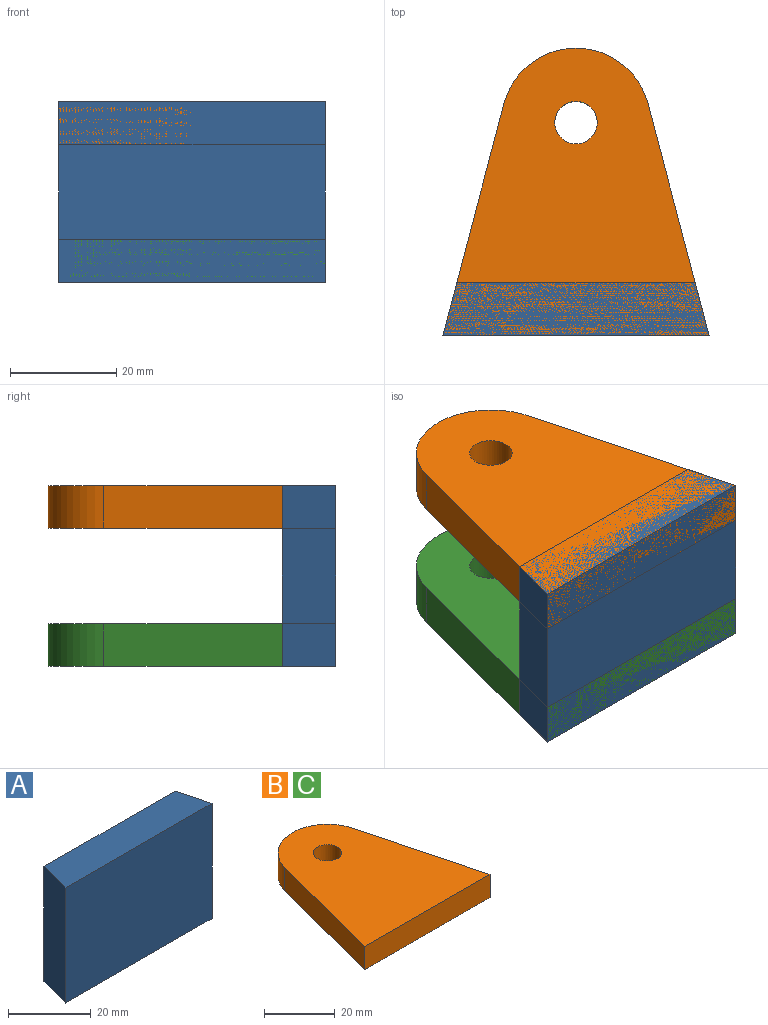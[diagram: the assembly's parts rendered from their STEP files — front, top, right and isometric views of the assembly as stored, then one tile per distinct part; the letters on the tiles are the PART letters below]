
ASSEMBLY  parts=3 mates=1
PART A: 9 faces, bbox 50x10x34 mm
  f0: plane 44.74x34mm, normal (0,1,0), area 1281.5mm2, adj f1,f2,f4,f5,f6,f7,f8
  f1: plane 34x10mm, normal (0.97,0.25,0), area 218.1mm2, adj f0,f3,f4,f5,f6,f7,f8
  f2: plane 34x10mm, normal (-0.97,0.25,0), area 351.6mm2, adj f0,f3,f4,f5
  f3: plane 50x34mm, normal (0,-1,0), area 1700mm2, adj f1,f2,f4,f5
  f4: plane 50x10mm, normal (0,0,1), area 473.7mm2, adj f0,f1,f2,f3
  f5: plane 50x10mm, normal (0,0,-1), area 473.7mm2, adj f0,f1,f2,f3
  f6: plane 17.09x8.07mm, normal (0,0,-1), area 60.4mm2, adj f0,f1,f8
  f7: plane 17.09x8.07mm, normal (0,0,1), area 60.4mm2, adj f0,f1,f8
  f8: plane 17.09x16mm, normal (0.43,0.9,0), area 302.4mm2, adj f0,f1,f6,f7
PART B: 7 faces, bbox 50x54x8 mm
  f0: plane 43.56x11.46mm, normal (0.97,0.25,0), area 360.4mm2, adj f1,f3,f5,f6
  f1: cylinder r=14mm len=27.08mm, axis (0,0,1), area 294.2mm2, adj f0,f2,f5,f6
  f2: plane 43.56x11.46mm, normal (-0.97,0.25,0), area 360.4mm2, adj f1,f3,f5,f6
  f3: plane 50x8mm, normal (0,-1,0), area 400mm2, adj f0,f2,f5,f6
  f4: cylinder r=4mm len=8mm, axis (0,0,1), area 201.1mm2, adj f5,f6
  f5: plane 54x50mm, normal (0,0,-1), area 1837.8mm2, adj f0,f1,f2,f3,f4
  f6: plane 54x50mm, normal (0,0,1), area 1837.8mm2, adj f0,f1,f2,f3,f4
PART C: same geometry as B
PLACE A t=(-25,40,-34)mm
PLACE B t=(-25,40,0)mm
PLACE C t=(-25,40,-26)mm
MATE fastened C.f5 <-> A.f5  axis (0,0,1) through (0,0,-34)mm
